FCSTD DOCUMENT  (FreeCAD 0.20R29603 (Git))
Label: edge-cuts
License: All rights reserved
LicenseURL: http://en.wikipedia.org/wiki/All_rights_reserved
objects: Sketcher::SketchObject×3, PartDesign::Body×1
note: 4 computed .brp shape members not serialized (recipe doc carries the construction recipe); baked Part::Feature solids carry a one-line shape summary decoded from their .brp

FEATURE [Sketcher::SketchObject] Sketch
  FullyConstrained = true
  MapMode = 5
  Support = -> [XY_Plane]
  sketch-geometry (35):
    g0: Circle CenterX=0 CenterY=0 CenterZ=0 NormalX=0 NormalY=0 NormalZ=1 AngleXU=0 Radius=34
    g1: Circle CenterX=30.15 CenterY=0 CenterZ=0 NormalX=0 NormalY=0 NormalZ=1 AngleXU=0 Radius=2.85
    g2: LineSegment StartX=30.15 StartY=0 StartZ=0 EndX=30.15 EndY=2.85 EndZ=0
    g3: LineSegment StartX=30.15 StartY=0 StartZ=0 EndX=30.15 EndY=-2.85 EndZ=0
    g4: ArcOfCircle CenterX=30.15 CenterY=0 CenterZ=0 NormalX=0 NormalY=0 NormalZ=1 AngleXU=0 Radius=2.85 StartAngle=1.5708 EndAngle=4.71239
    g5: GeomPoint X=34 Y=0 Z=0
    g6: GeomPoint X=33 Y=0 Z=0
    g7: Circle CenterX=14 CenterY=30.9839 CenterZ=0 NormalX=0 NormalY=0 NormalZ=1 AngleXU=0 Radius=2.15
    g8: Circle CenterX=0 CenterY=0 CenterZ=0 NormalX=0 NormalY=0 NormalZ=1 AngleXU=0 Radius=32.5
    g9: GeomPoint X=4.625 Y=33.684 Z=0
    g10: ArcOfCircle CenterX=8.08202 CenterY=28.684 CenterZ=0 NormalX=0 NormalY=0 NormalZ=1 AngleXU=0 Radius=4.19918 StartAngle=0.370665 EndAngle=1.29616
    g11: ArcOfCircle CenterX=2.918e-13 CenterY=1.5156e-12 CenterZ=0 NormalX=0 NormalY=0 NormalZ=1 AngleXU=0 Radius=34 StartAngle=1.29616 EndAngle=1.43434
    g12: ArcOfCircle CenterX=14.6946 CenterY=28.4265 CenterZ=0 NormalX=0 NormalY=0 NormalZ=1 AngleXU=0 Radius=0.5 StartAngle=1.09369 EndAngle=1.83602
    g13: LineSegment StartX=14.6946 StartY=28.4265 StartZ=0 EndX=14.9242 EndY=28.8707 EndZ=0
    g14: LineSegment StartX=14.6946 StartY=28.4265 StartZ=0 EndX=14.5636 EndY=28.909 EndZ=0
    g15: ArcOfCircle CenterX=30.15 CenterY=4.81754 CenterZ=0 NormalX=0 NormalY=0 NormalZ=1 AngleXU=0 Radius=1.96754 StartAngle=4.71239 EndAngle=6.44163
    g16: LineSegment StartX=30.15 StartY=4.81754 StartZ=0 EndX=32.0929 EndY=5.12799 EndZ=0
    g17: ArcOfCircle CenterX=14 CenterY=30.9839 CenterZ=0 NormalX=0 NormalY=0 NormalZ=1 AngleXU=0 Radius=2.15 StartAngle=3.51226 EndAngle=4.97762
    g18: ArcOfCircle CenterX=30.15 CenterY=-4.81754 CenterZ=0 NormalX=0 NormalY=0 NormalZ=1 AngleXU=0 Radius=1.96754 StartAngle=6.12474 EndAngle=7.85398
    g19: LineSegment StartX=30.15 StartY=-4.81754 StartZ=0 EndX=32.0929 EndY=-5.12799 EndZ=0
    g20: LineSegment StartX=8.08202 StartY=28.684 StartZ=0 EndX=11.996 EndY=30.2051 EndZ=0
    g21: LineSegment StartX=8.08202 StartY=28.684 StartZ=0 EndX=9.22084 EndY=32.7258 EndZ=0
    g22: GeomPoint X=-1.2e-14 Y=-32.5 Z=0
    g23: LineSegment StartX=30.15 StartY=4.81754 StartZ=0 EndX=30.15 EndY=2.85 EndZ=0
    g24: LineSegment StartX=30.15 StartY=-4.81754 StartZ=0 EndX=30.15 EndY=-2.85 EndZ=0
    g25: LineSegment StartX=19.9592 StartY=25.6491 StartZ=0 EndX=25.6491 EndY=19.9592 EndZ=0
    g26: LineSegment StartX=22.8042 StartY=22.8042 StartZ=0 EndX=22.981 EndY=22.981 EndZ=0
    g27: LineSegment StartX=22.8042 StartY=22.8042 StartZ=0 EndX=2.913e-13 EndY=1.517e-12 EndZ=0
    g28: LineSegment StartX=25.6491 StartY=-19.9592 StartZ=0 EndX=19.9592 EndY=-25.6491 EndZ=0
    g29: LineSegment StartX=22.8042 StartY=-22.8042 StartZ=0 EndX=22.981 EndY=-22.981 EndZ=0
    g30: LineSegment StartX=2.918e-13 StartY=1.5156e-12 StartZ=0 EndX=22.8042 EndY=-22.8042 EndZ=0
    g31: ArcOfCircle CenterX=-3.2e-14 CenterY=-9.91e-14 CenterZ=0 NormalX=0 NormalY=0 NormalZ=1 AngleXU=0 Radius=32.5 StartAngle=0.909513 EndAngle=1.09369
    g32: ArcOfCircle CenterX=-6.88e-14 CenterY=-2.1e-14 CenterZ=0 NormalX=0 NormalY=0 NormalZ=1 AngleXU=0 Radius=32.5 StartAngle=0.158446 EndAngle=0.661284
    g33: ArcOfCircle CenterX=-3.37e-14 CenterY=-2.1e-15 CenterZ=0 NormalX=0 NormalY=0 NormalZ=1 AngleXU=0 Radius=32.5 StartAngle=5.6219 EndAngle=6.12474
    g34: ArcOfCircle CenterX=2.28e-14 CenterY=-9.54e-14 CenterZ=0 NormalX=0 NormalY=0 NormalZ=1 AngleXU=0 Radius=32.5 StartAngle=4.71239 EndAngle=5.37367
  constraints (98):
    c: Coincident(g0,g-1)
    c: Radius(g0) = 34
    c: PointOnObject(g1,g-1)
    c: Diameter(g1) = 5.7
    c: PointOnObject(g2,g1)
    c: Coincident(g2,g1)
    c: Vertical(g2)
    c: Coincident(g3,g1)
    c: PointOnObject(g5,g0)
    c: PointOnObject(g5,g-1)
    c: Coincident(g4,g1)
    c: Vertical(g3)
    c: PointOnObject(g6,g1)
    c: PointOnObject(g6,g-1)
    c: PointOnObject(g7,g0)
    c: Diameter(g7) = 4.3
    c: Coincident(g8,g0)
    c: Radius(g8) = 32.5
    c: PointOnObject(g9,g0)
    c: DistanceX(g-1,g9) = 4.625
    c: DistanceX(g-1,g7) = 14
    c: PointOnObject(g10,g8)
    c: PointOnObject(g10,g0)
    c: PointOnObject(g10,g7)
    c: Coincident(g11,g10)
    c: Coincident(g11,g9)
    c: Tangent(g11,g0)
    c: PointOnObject(g12,g8)
    c: PointOnObject(g12,g7)
    c: Coincident(g13,g12)
    c: Coincident(g13,g12)
    c: Coincident(g14,g12)
    c: Coincident(g14,g12)
    c: Perpendicular(g7,g14)
    c: Perpendicular(g8,g13)
    c: Coincident(g4,g2)
    c: Coincident(g4,g3)
    c: PointOnObject(g15,g8)
    c: Coincident(g16,g15)
    c: Coincident(g16,g15)
    c: Perpendicular(g8,g16)
    c: Radius(g12) = 0.5
    c: Coincident(g17,g10)
    c: Coincident(g17,g12)
    c: DistanceX(g4,g5) = 3.85
    c: PointOnObject(g18,g8)
    c: Coincident(g19,g18)
    c: Coincident(g19,g18)
    c: Perpendicular(g8,g19)
    c: Coincident(g20,g10)
    c: Coincident(g20,g10)
    c: Perpendicular(g17,g20)
    c: Coincident(g21,g10)
    c: Coincident(g21,g10)
    c: Perpendicular(g11,g21)
    c: PointOnObject(g22,g-2)
    c: PointOnObject(g22,g8)
    c: Coincident(g15,g4)
    c: Coincident(g23,g15)
    c: Coincident(g23,g4)
    c: Perpendicular(g4,g23)
    c: Coincident(g18,g4)
    c: Coincident(g24,g18)
    c: Coincident(g24,g4)
    c: Perpendicular(g4,g24)
    c: PointOnObject(g25,g8)
    c: PointOnObject(g25,g8)
    c: PointOnObject(g26,g25)
    c: PointOnObject(g26,g8)
    c: Perpendicular(g25,g26)
    c: Distance(g26) = 0.25
    c: Coincident(g27,g26)
    c: Coincident(g27,g11)
    c: Parallel(g27,g26)
    c: Angle(g-1,g27) = 0.785398
    c: PointOnObject(g28,g8)
    c: PointOnObject(g28,g8)
    c: PointOnObject(g29,g28)
    c: PointOnObject(g29,g8)
    c: Perpendicular(g28,g29)
    c: Equal(g29,g26)
    c: Coincident(g30,g11)
    c: Coincident(g30,g29)
    c: Parallel(g30,g29)
    c: Angle(g30,g-1) = 0.785398
    c: Coincident(g31,g12)
    c: Coincident(g31,g25)
    c: Tangent(g31,g8)
    c: Coincident(g32,g25)
    c: Coincident(g32,g15)
    c: Tangent(g32,g8)
    c: Coincident(g33,g18)
    c: Coincident(g33,g28)
    c: Tangent(g33,g8)
    c: Coincident(g34,g28)
    c: Coincident(g34,g22)
    c: Tangent(g34,g8)
    c: Tangent(g17,g7)
FEATURE [PartDesign::Body] Body  label="Shape"
  Group = -> [Sketch]
  Origin = -> Origin
FEATURE [Sketcher::SketchObject] MirroredSketch
  FullyConstrained = false
  sketch-geometry (35):
    g0: Circle CenterX=0 CenterY=0 CenterZ=0 NormalX=0 NormalY=0 NormalZ=1 AngleXU=0 Radius=34
    g1: Circle CenterX=-30.15 CenterY=0 CenterZ=0 NormalX=0 NormalY=0 NormalZ=1 AngleXU=0 Radius=2.85
    g2: LineSegment StartX=-30.15 StartY=0 StartZ=0 EndX=-30.15 EndY=2.85 EndZ=0
    g3: LineSegment StartX=-30.15 StartY=0 StartZ=0 EndX=-30.15 EndY=-2.85 EndZ=0
    g4: ArcOfCircle CenterX=-30.15 CenterY=0 CenterZ=0 NormalX=0 NormalY=0 NormalZ=1 AngleXU=0 Radius=2.85 StartAngle=4.71239 EndAngle=7.85398
    g5: GeomPoint X=-34 Y=0 Z=0
    g6: GeomPoint X=-33 Y=0 Z=0
    g7: Circle CenterX=-14 CenterY=30.9839 CenterZ=0 NormalX=0 NormalY=0 NormalZ=1 AngleXU=0 Radius=2.15
    g8: Circle CenterX=0 CenterY=0 CenterZ=0 NormalX=0 NormalY=0 NormalZ=1 AngleXU=0 Radius=32.5
    g9: GeomPoint X=-4.625 Y=33.684 Z=0
    g10: ArcOfCircle CenterX=-8.08202 CenterY=28.684 CenterZ=0 NormalX=0 NormalY=0 NormalZ=1 AngleXU=0 Radius=4.19918 StartAngle=1.84544 EndAngle=2.77093
    g11: ArcOfCircle CenterX=-2.913e-13 CenterY=1.517e-12 CenterZ=0 NormalX=0 NormalY=0 NormalZ=1 AngleXU=0 Radius=34 StartAngle=1.70725 EndAngle=1.84544
    g12: ArcOfCircle CenterX=-14.6946 CenterY=28.4265 CenterZ=0 NormalX=0 NormalY=0 NormalZ=1 AngleXU=0 Radius=0.5 StartAngle=1.30557 EndAngle=2.0479
    g13: LineSegment StartX=-14.6946 StartY=28.4265 StartZ=0 EndX=-14.9242 EndY=28.8707 EndZ=0
    g14: LineSegment StartX=-14.6946 StartY=28.4265 StartZ=0 EndX=-14.5636 EndY=28.909 EndZ=0
    g15: ArcOfCircle CenterX=-30.15 CenterY=4.81754 CenterZ=0 NormalX=0 NormalY=0 NormalZ=1 AngleXU=0 Radius=1.96754 StartAngle=2.98315 EndAngle=4.71239
    g16: LineSegment StartX=-30.15 StartY=4.81754 StartZ=0 EndX=-32.0929 EndY=5.12799 EndZ=0
    g17: ArcOfCircle CenterX=-14 CenterY=30.9839 CenterZ=0 NormalX=0 NormalY=0 NormalZ=1 AngleXU=0 Radius=2.15 StartAngle=4.44716 EndAngle=5.91252
    g18: ArcOfCircle CenterX=-30.15 CenterY=-4.81754 CenterZ=0 NormalX=0 NormalY=0 NormalZ=1 AngleXU=0 Radius=1.96754 StartAngle=1.5708 EndAngle=3.30004
    g19: LineSegment StartX=-30.15 StartY=-4.81754 StartZ=0 EndX=-32.0929 EndY=-5.12799 EndZ=0
    g20: LineSegment StartX=-8.08202 StartY=28.684 StartZ=0 EndX=-11.996 EndY=30.2051 EndZ=0
    g21: LineSegment StartX=-8.08202 StartY=28.684 StartZ=0 EndX=-9.22084 EndY=32.7258 EndZ=0
    g22: GeomPoint X=1.2e-14 Y=-32.5 Z=0
    g23: LineSegment StartX=-30.15 StartY=4.81754 StartZ=0 EndX=-30.15 EndY=2.85 EndZ=0
    g24: LineSegment StartX=-30.15 StartY=-4.81754 StartZ=0 EndX=-30.15 EndY=-2.85 EndZ=0
    g25: LineSegment StartX=-19.9592 StartY=25.6491 StartZ=0 EndX=-25.6491 EndY=19.9592 EndZ=0
    g26: LineSegment StartX=-22.8042 StartY=22.8042 StartZ=0 EndX=-22.981 EndY=22.981 EndZ=0
    g27: LineSegment StartX=-22.8042 StartY=22.8042 StartZ=0 EndX=-2.913e-13 EndY=1.517e-12 EndZ=0
    g28: LineSegment StartX=-25.6491 StartY=-19.9592 StartZ=0 EndX=-19.9592 EndY=-25.6491 EndZ=0
    g29: LineSegment StartX=-22.8042 StartY=-22.8042 StartZ=0 EndX=-22.981 EndY=-22.981 EndZ=0
    g30: LineSegment StartX=-2.913e-13 StartY=1.517e-12 StartZ=0 EndX=-22.8042 EndY=-22.8042 EndZ=0
    g31: ArcOfCircle CenterX=3.2e-14 CenterY=-9.91e-14 CenterZ=0 NormalX=0 NormalY=0 NormalZ=1 AngleXU=0 Radius=32.5 StartAngle=2.0479 EndAngle=2.23208
    g32: ArcOfCircle CenterX=6.88e-14 CenterY=-2.1e-14 CenterZ=0 NormalX=0 NormalY=0 NormalZ=1 AngleXU=0 Radius=32.5 StartAngle=2.48031 EndAngle=2.98315
    g33: ArcOfCircle CenterX=3.37e-14 CenterY=-2.1e-15 CenterZ=0 NormalX=0 NormalY=0 NormalZ=1 AngleXU=0 Radius=32.5 StartAngle=3.30004 EndAngle=3.80288
    g34: ArcOfCircle CenterX=-2.28e-14 CenterY=-9.54e-14 CenterZ=0 NormalX=0 NormalY=0 NormalZ=1 AngleXU=0 Radius=32.5 StartAngle=4.05111 EndAngle=4.71239
  constraints (88):
    c: Radius(g0) = 34
    c: Diameter(g1) = 5.7
    c: PointOnObject(g2,g1)
    c: Coincident(g2,g1)
    c: Vertical(g2)
    c: Coincident(g3,g1)
    c: PointOnObject(g5,g0)
    c: Coincident(g4,g1)
    c: Vertical(g3)
    c: PointOnObject(g6,g1)
    c: PointOnObject(g7,g0)
    c: Diameter(g7) = 4.3
    c: Coincident(g8,g0)
    c: Radius(g8) = 32.5
    c: PointOnObject(g9,g0)
    c: PointOnObject(g10,g8)
    c: PointOnObject(g10,g0)
    c: PointOnObject(g10,g7)
    c: Coincident(g11,g10)
    c: Coincident(g11,g9)
    c: Tangent(g11,g0)
    c: PointOnObject(g12,g8)
    c: PointOnObject(g12,g7)
    c: Coincident(g13,g12)
    c: Coincident(g13,g12)
    c: Coincident(g14,g12)
    c: Coincident(g14,g12)
    c: Perpendicular(g7,g14)
    c: Perpendicular(g8,g13)
    c: Coincident(g4,g2)
    c: Coincident(g4,g3)
    c: PointOnObject(g15,g8)
    c: Coincident(g16,g15)
    c: Coincident(g16,g15)
    c: Perpendicular(g8,g16)
    c: Radius(g12) = 0.5
    c: Coincident(g17,g10)
    c: Coincident(g17,g12)
    c: PointOnObject(g18,g8)
    c: Coincident(g19,g18)
    c: Coincident(g19,g18)
    c: Perpendicular(g8,g19)
    c: Coincident(g20,g10)
    c: Coincident(g20,g10)
    c: Perpendicular(g17,g20)
    c: Coincident(g21,g10)
    c: Coincident(g21,g10)
    c: Perpendicular(g11,g21)
    c: PointOnObject(g22,g8)
    c: Coincident(g15,g4)
    c: Coincident(g23,g15)
    c: Coincident(g23,g4)
    c: Perpendicular(g4,g23)
    c: Coincident(g18,g4)
    c: Coincident(g24,g18)
    c: Coincident(g24,g4)
    c: Perpendicular(g4,g24)
    c: PointOnObject(g25,g8)
    c: PointOnObject(g25,g8)
    c: PointOnObject(g26,g25)
    c: PointOnObject(g26,g8)
    c: Perpendicular(g25,g26)
    c: Distance(g26) = 0.25
    c: Coincident(g27,g26)
    c: Coincident(g27,g11)
    c: Parallel(g27,g26)
    c: PointOnObject(g28,g8)
    c: PointOnObject(g28,g8)
    c: PointOnObject(g29,g28)
    c: PointOnObject(g29,g8)
    c: Perpendicular(g28,g29)
    c: Equal(g29,g26)
    c: Coincident(g30,g11)
    c: Coincident(g30,g29)
    c: Parallel(g30,g29)
    c: Coincident(g31,g12)
    c: Coincident(g31,g25)
    c: Tangent(g31,g8)
    c: Coincident(g32,g25)
    c: Coincident(g32,g15)
    c: Tangent(g32,g8)
    c: Coincident(g33,g18)
    c: Coincident(g33,g28)
    c: Tangent(g33,g8)
    c: Coincident(g34,g28)
    c: Coincident(g34,g22)
    c: Tangent(g34,g8)
    c: Tangent(g17,g7)
FEATURE [Sketcher::SketchObject] Sketch001
  FullyConstrained = false
  sketch-geometry (70):
    g0: Circle CenterX=0 CenterY=0 CenterZ=0 NormalX=0 NormalY=0 NormalZ=1 AngleXU=0 Radius=34
    g1: Circle CenterX=-30.15 CenterY=0 CenterZ=0 NormalX=0 NormalY=0 NormalZ=1 AngleXU=0 Radius=2.85
    g2: LineSegment StartX=-30.15 StartY=0 StartZ=0 EndX=-30.15 EndY=2.85 EndZ=0
    g3: LineSegment StartX=-30.15 StartY=0 StartZ=0 EndX=-30.15 EndY=-2.85 EndZ=0
    g4: ArcOfCircle CenterX=-30.15 CenterY=0 CenterZ=0 NormalX=0 NormalY=0 NormalZ=1 AngleXU=0 Radius=2.85 StartAngle=4.71239 EndAngle=7.85398
    g5: GeomPoint X=-34 Y=0 Z=0
    g6: GeomPoint X=-33 Y=0 Z=0
    g7: Circle CenterX=-14 CenterY=30.9839 CenterZ=0 NormalX=0 NormalY=0 NormalZ=1 AngleXU=0 Radius=2.15
    g8: Circle CenterX=0 CenterY=0 CenterZ=0 NormalX=0 NormalY=0 NormalZ=1 AngleXU=0 Radius=32.5
    g9: GeomPoint X=-4.625 Y=33.684 Z=0
    g10: ArcOfCircle CenterX=-8.08202 CenterY=28.684 CenterZ=0 NormalX=0 NormalY=0 NormalZ=1 AngleXU=0 Radius=4.19918 StartAngle=1.84544 EndAngle=2.77093
    g11: ArcOfCircle CenterX=-2.913e-13 CenterY=1.517e-12 CenterZ=0 NormalX=0 NormalY=0 NormalZ=1 AngleXU=0 Radius=34 StartAngle=1.70725 EndAngle=1.84544
    g12: ArcOfCircle CenterX=-14.6946 CenterY=28.4265 CenterZ=0 NormalX=0 NormalY=0 NormalZ=1 AngleXU=0 Radius=0.5 StartAngle=1.30557 EndAngle=2.0479
    g13: LineSegment StartX=-14.6946 StartY=28.4265 StartZ=0 EndX=-14.9242 EndY=28.8707 EndZ=0
    g14: LineSegment StartX=-14.6946 StartY=28.4265 StartZ=0 EndX=-14.5636 EndY=28.909 EndZ=0
    g15: ArcOfCircle CenterX=-30.15 CenterY=4.81754 CenterZ=0 NormalX=0 NormalY=0 NormalZ=1 AngleXU=0 Radius=1.96754 StartAngle=2.98315 EndAngle=4.71239
    g16: LineSegment StartX=-30.15 StartY=4.81754 StartZ=0 EndX=-32.0929 EndY=5.12799 EndZ=0
    g17: ArcOfCircle CenterX=-14 CenterY=30.9839 CenterZ=0 NormalX=0 NormalY=0 NormalZ=1 AngleXU=0 Radius=2.15 StartAngle=4.44716 EndAngle=5.91252
    g18: ArcOfCircle CenterX=-30.15 CenterY=-4.81754 CenterZ=0 NormalX=0 NormalY=0 NormalZ=1 AngleXU=0 Radius=1.96754 StartAngle=1.5708 EndAngle=3.30004
    g19: LineSegment StartX=-30.15 StartY=-4.81754 StartZ=0 EndX=-32.0929 EndY=-5.12799 EndZ=0
    g20: LineSegment StartX=-8.08202 StartY=28.684 StartZ=0 EndX=-11.996 EndY=30.2051 EndZ=0
    g21: LineSegment StartX=-8.08202 StartY=28.684 StartZ=0 EndX=-9.22084 EndY=32.7258 EndZ=0
    g22: GeomPoint X=1e-16 Y=-32.5 Z=0
    g23: LineSegment StartX=-30.15 StartY=4.81754 StartZ=0 EndX=-30.15 EndY=2.85 EndZ=0
    g24: LineSegment StartX=-30.15 StartY=-4.81754 StartZ=0 EndX=-30.15 EndY=-2.85 EndZ=0
    g25: LineSegment StartX=-19.9592 StartY=25.6491 StartZ=0 EndX=-25.6491 EndY=19.9592 EndZ=0
    g26: LineSegment StartX=-22.8042 StartY=22.8042 StartZ=0 EndX=-22.981 EndY=22.981 EndZ=0
    g27: LineSegment StartX=-22.8042 StartY=22.8042 StartZ=0 EndX=-2.913e-13 EndY=1.517e-12 EndZ=0
    g28: LineSegment StartX=-25.6491 StartY=-19.9592 StartZ=0 EndX=-19.9592 EndY=-25.6491 EndZ=0
    g29: LineSegment StartX=-22.8042 StartY=-22.8042 StartZ=0 EndX=-22.981 EndY=-22.981 EndZ=0
    g30: LineSegment StartX=-2.913e-13 StartY=1.517e-12 StartZ=0 EndX=-22.8042 EndY=-22.8042 EndZ=0
    g31: ArcOfCircle CenterX=3.2e-14 CenterY=-9.91e-14 CenterZ=0 NormalX=0 NormalY=0 NormalZ=1 AngleXU=0 Radius=32.5 StartAngle=2.0479 EndAngle=2.23208
    g32: ArcOfCircle CenterX=6.88e-14 CenterY=-2.1e-14 CenterZ=0 NormalX=0 NormalY=0 NormalZ=1 AngleXU=0 Radius=32.5 StartAngle=2.48031 EndAngle=2.98315
    g33: ArcOfCircle CenterX=3.37e-14 CenterY=-2.1e-15 CenterZ=0 NormalX=0 NormalY=0 NormalZ=1 AngleXU=0 Radius=32.5 StartAngle=3.30004 EndAngle=3.80288
    g34: ArcOfCircle CenterX=-2.28e-14 CenterY=-9.54e-14 CenterZ=0 NormalX=0 NormalY=0 NormalZ=1 AngleXU=0 Radius=32.5 StartAngle=4.05111 EndAngle=4.71239
    g35: Circle CenterX=0 CenterY=0 CenterZ=0 NormalX=0 NormalY=0 NormalZ=1 AngleXU=0 Radius=34
    g36: Circle CenterX=30.15 CenterY=0 CenterZ=0 NormalX=0 NormalY=0 NormalZ=1 AngleXU=0 Radius=2.85
    g37: LineSegment StartX=30.15 StartY=0 StartZ=0 EndX=30.15 EndY=2.85 EndZ=0
    g38: LineSegment StartX=30.15 StartY=0 StartZ=0 EndX=30.15 EndY=-2.85 EndZ=0
    g39: ArcOfCircle CenterX=30.15 CenterY=0 CenterZ=0 NormalX=0 NormalY=0 NormalZ=1 AngleXU=0 Radius=2.85 StartAngle=1.5708 EndAngle=4.71239
    g40: GeomPoint X=34 Y=0 Z=0
    g41: GeomPoint X=33 Y=0 Z=0
    g42: Circle CenterX=14 CenterY=30.9839 CenterZ=0 NormalX=0 NormalY=0 NormalZ=1 AngleXU=0 Radius=2.15
    g43: Circle CenterX=0 CenterY=0 CenterZ=0 NormalX=0 NormalY=0 NormalZ=1 AngleXU=0 Radius=32.5
    g44: GeomPoint X=4.625 Y=33.684 Z=0
    g45: ArcOfCircle CenterX=8.08202 CenterY=28.684 CenterZ=0 NormalX=0 NormalY=0 NormalZ=1 AngleXU=0 Radius=4.19918 StartAngle=0.370665 EndAngle=1.29616
    g46: ArcOfCircle CenterX=2.918e-13 CenterY=1.5156e-12 CenterZ=0 NormalX=0 NormalY=0 NormalZ=1 AngleXU=0 Radius=34 StartAngle=1.29616 EndAngle=1.43434
    g47: ArcOfCircle CenterX=14.6946 CenterY=28.4265 CenterZ=0 NormalX=0 NormalY=0 NormalZ=1 AngleXU=0 Radius=0.5 StartAngle=1.09369 EndAngle=1.83602
    g48: LineSegment StartX=14.6946 StartY=28.4265 StartZ=0 EndX=14.9242 EndY=28.8707 EndZ=0
    g49: LineSegment StartX=14.6946 StartY=28.4265 StartZ=0 EndX=14.5636 EndY=28.909 EndZ=0
    g50: ArcOfCircle CenterX=30.15 CenterY=4.81754 CenterZ=0 NormalX=0 NormalY=0 NormalZ=1 AngleXU=0 Radius=1.96754 StartAngle=4.71239 EndAngle=6.44163
    g51: LineSegment StartX=30.15 StartY=4.81754 StartZ=0 EndX=32.0929 EndY=5.12799 EndZ=0
    g52: ArcOfCircle CenterX=14 CenterY=30.9839 CenterZ=0 NormalX=0 NormalY=0 NormalZ=1 AngleXU=0 Radius=2.15 StartAngle=3.51226 EndAngle=4.97762
    g53: ArcOfCircle CenterX=30.15 CenterY=-4.81754 CenterZ=0 NormalX=0 NormalY=0 NormalZ=1 AngleXU=0 Radius=1.96754 StartAngle=6.12474 EndAngle=7.85398
    g54: LineSegment StartX=30.15 StartY=-4.81754 StartZ=0 EndX=32.0929 EndY=-5.12799 EndZ=0
    g55: LineSegment StartX=8.08202 StartY=28.684 StartZ=0 EndX=11.996 EndY=30.2051 EndZ=0
    g56: LineSegment StartX=8.08202 StartY=28.684 StartZ=0 EndX=9.22084 EndY=32.7258 EndZ=0
    g57: GeomPoint X=-1.2e-14 Y=-32.5 Z=0
    g58: LineSegment StartX=30.15 StartY=4.81754 StartZ=0 EndX=30.15 EndY=2.85 EndZ=0
    g59: LineSegment StartX=30.15 StartY=-4.81754 StartZ=0 EndX=30.15 EndY=-2.85 EndZ=0
    g60: LineSegment StartX=19.9592 StartY=25.6491 StartZ=0 EndX=25.6491 EndY=19.9592 EndZ=0
    g61: LineSegment StartX=22.8042 StartY=22.8042 StartZ=0 EndX=22.981 EndY=22.981 EndZ=0
    g62: LineSegment StartX=22.8042 StartY=22.8042 StartZ=0 EndX=2.913e-13 EndY=1.517e-12 EndZ=0
    g63: LineSegment StartX=25.6491 StartY=-19.9592 StartZ=0 EndX=19.9592 EndY=-25.6491 EndZ=0
    g64: LineSegment StartX=22.8042 StartY=-22.8042 StartZ=0 EndX=22.981 EndY=-22.981 EndZ=0
    g65: LineSegment StartX=2.918e-13 StartY=1.5156e-12 StartZ=0 EndX=22.8042 EndY=-22.8042 EndZ=0
    g66: ArcOfCircle CenterX=-3.2e-14 CenterY=-9.91e-14 CenterZ=0 NormalX=0 NormalY=0 NormalZ=1 AngleXU=0 Radius=32.5 StartAngle=0.909513 EndAngle=1.09369
    g67: ArcOfCircle CenterX=-6.88e-14 CenterY=-2.1e-14 CenterZ=0 NormalX=0 NormalY=0 NormalZ=1 AngleXU=0 Radius=32.5 StartAngle=0.158446 EndAngle=0.661284
    g68: ArcOfCircle CenterX=-3.37e-14 CenterY=-2.1e-15 CenterZ=0 NormalX=0 NormalY=0 NormalZ=1 AngleXU=0 Radius=32.5 StartAngle=5.6219 EndAngle=6.12474
    g69: ArcOfCircle CenterX=2.28e-14 CenterY=-9.54e-14 CenterZ=0 NormalX=0 NormalY=0 NormalZ=1 AngleXU=0 Radius=32.5 StartAngle=4.71239 EndAngle=5.37367
  constraints (186):
    c: Radius(g0) = 34
    c: Diameter(g1) = 5.7
    c: PointOnObject(g2,g1)
    c: Coincident(g2,g1)
    c: Vertical(g2)
    c: Coincident(g3,g1)
    c: PointOnObject(g5,g0)
    c: Coincident(g4,g1)
    c: Vertical(g3)
    c: PointOnObject(g6,g1)
    c: PointOnObject(g7,g0)
    c: Diameter(g7) = 4.3
    c: Coincident(g8,g0)
    c: Radius(g8) = 32.5
    c: PointOnObject(g9,g0)
    c: PointOnObject(g10,g8)
    c: PointOnObject(g10,g0)
    c: PointOnObject(g10,g7)
    c: Coincident(g11,g10)
    c: Coincident(g11,g9)
    c: Tangent(g11,g0)
    c: PointOnObject(g12,g8)
    c: PointOnObject(g12,g7)
    c: Coincident(g13,g12)
    c: Coincident(g13,g12)
    c: Coincident(g14,g12)
    c: Coincident(g14,g12)
    c: Perpendicular(g7,g14)
    c: Perpendicular(g8,g13)
    c: Coincident(g4,g2)
    c: Coincident(g4,g3)
    c: PointOnObject(g15,g8)
    c: Coincident(g16,g15)
    c: Coincident(g16,g15)
    c: Perpendicular(g8,g16)
    c: Radius(g12) = 0.5
    c: Coincident(g17,g10)
    c: Coincident(g17,g12)
    c: PointOnObject(g18,g8)
    c: Coincident(g19,g18)
    c: Coincident(g19,g18)
    c: Perpendicular(g8,g19)
    c: Coincident(g20,g10)
    c: Coincident(g20,g10)
    c: Perpendicular(g17,g20)
    c: Coincident(g21,g10)
    c: Coincident(g21,g10)
    c: Perpendicular(g11,g21)
    c: PointOnObject(g22,g8)
    c: Coincident(g15,g4)
    c: Coincident(g23,g15)
    c: Coincident(g23,g4)
    c: Perpendicular(g4,g23)
    c: Coincident(g18,g4)
    c: Coincident(g24,g18)
    c: Coincident(g24,g4)
    c: Perpendicular(g4,g24)
    c: PointOnObject(g25,g8)
    c: PointOnObject(g25,g8)
    c: PointOnObject(g26,g25)
    c: PointOnObject(g26,g8)
    c: Perpendicular(g25,g26)
    c: Distance(g26) = 0.25
    c: Coincident(g27,g26)
    c: Coincident(g27,g11)
    c: Parallel(g27,g26)
    c: PointOnObject(g28,g8)
    c: PointOnObject(g28,g8)
    c: PointOnObject(g29,g28)
    c: PointOnObject(g29,g8)
    c: Perpendicular(g28,g29)
    c: Equal(g29,g26)
    c: Coincident(g30,g11)
    c: Coincident(g30,g29)
    c: Parallel(g30,g29)
    c: Coincident(g31,g12)
    c: Coincident(g31,g25)
    c: Tangent(g31,g8)
    c: Coincident(g32,g25)
    c: Coincident(g32,g15)
    c: Tangent(g32,g8)
    c: Coincident(g33,g18)
    c: Coincident(g33,g28)
    c: Tangent(g33,g8)
    c: Coincident(g34,g28)
    c: Coincident(g34,g22)
    c: Tangent(g34,g8)
    c: Tangent(g17,g7)
    c: Coincident(g35,g-1)
    c: Radius(g35) = 34
    c: PointOnObject(g36,g-1)
    c: Diameter(g36) = 5.7
    c: PointOnObject(g37,g36)
    c: Coincident(g37,g36)
    c: Vertical(g37)
    c: Coincident(g38,g36)
    c: PointOnObject(g40,g35)
    c: PointOnObject(g40,g-1)
    c: Coincident(g39,g36)
    c: Vertical(g38)
    c: PointOnObject(g41,g36)
    c: PointOnObject(g41,g-1)
    c: PointOnObject(g42,g35)
    c: Diameter(g42) = 4.3
    c: Coincident(g43,g35)
    c: Radius(g43) = 32.5
    c: PointOnObject(g44,g35)
    c: DistanceX(g-1,g44) = 4.625
    c: DistanceX(g-1,g42) = 14
    c: PointOnObject(g45,g43)
    c: PointOnObject(g45,g35)
    c: PointOnObject(g45,g42)
    c: Coincident(g46,g45)
    c: Coincident(g46,g44)
    c: Tangent(g46,g35)
    c: PointOnObject(g47,g43)
    c: PointOnObject(g47,g42)
    c: Coincident(g48,g47)
    c: Coincident(g48,g47)
    c: Coincident(g49,g47)
    c: Coincident(g49,g47)
    c: Perpendicular(g42,g49)
    c: Perpendicular(g43,g48)
    c: Coincident(g39,g37)
    c: Coincident(g39,g38)
    c: PointOnObject(g50,g43)
    c: Coincident(g51,g50)
    c: Coincident(g51,g50)
    c: Perpendicular(g43,g51)
    c: Radius(g47) = 0.5
    c: Coincident(g52,g45)
    c: Coincident(g52,g47)
    c: DistanceX(g39,g40) = 3.85
    c: PointOnObject(g53,g43)
    c: Coincident(g54,g53)
    c: Coincident(g54,g53)
    c: Perpendicular(g43,g54)
    c: Coincident(g55,g45)
    c: Coincident(g55,g45)
    c: Perpendicular(g52,g55)
    c: Coincident(g56,g45)
    c: Coincident(g56,g45)
    c: Perpendicular(g46,g56)
    c: PointOnObject(g57,g-2)
    c: PointOnObject(g57,g43)
    c: Coincident(g50,g39)
    c: Coincident(g58,g50)
    c: Coincident(g58,g39)
    c: Perpendicular(g39,g58)
    c: Coincident(g53,g39)
    c: Coincident(g59,g53)
    c: Coincident(g59,g39)
    c: Perpendicular(g39,g59)
    c: PointOnObject(g60,g43)
    c: PointOnObject(g60,g43)
    c: PointOnObject(g61,g60)
    c: PointOnObject(g61,g43)
    c: Perpendicular(g60,g61)
    c: Distance(g61) = 0.25
    c: Coincident(g62,g61)
    c: Coincident(g62,g46)
    c: Parallel(g62,g61)
    c: Angle(g-1,g62) = 0.785398
    c: PointOnObject(g63,g43)
    c: PointOnObject(g63,g43)
    c: PointOnObject(g64,g63)
    c: PointOnObject(g64,g43)
    c: Perpendicular(g63,g64)
    c: Equal(g64,g61)
    c: Coincident(g65,g46)
    c: Coincident(g65,g64)
    c: Parallel(g65,g64)
    c: Angle(g65,g-1) = 0.785398
    c: Coincident(g66,g47)
    c: Coincident(g66,g60)
    c: Tangent(g66,g43)
    c: Coincident(g67,g60)
    c: Coincident(g67,g50)
    c: Tangent(g67,g43)
    c: Coincident(g68,g53)
    c: Coincident(g68,g63)
    c: Tangent(g68,g43)
    c: Coincident(g69,g63)
    c: Coincident(g69,g57)
    c: Tangent(g69,g43)
    c: Tangent(g52,g42)
